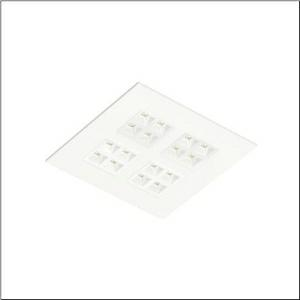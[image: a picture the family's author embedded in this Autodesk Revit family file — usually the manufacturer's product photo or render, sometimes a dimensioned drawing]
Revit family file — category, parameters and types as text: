
# Revit family: silica_r__31_square_51my6ndu34wa_7304
name_source: partatom
category: Lighting Fixtures
units: mm (PartAtom-declared; Revit-internal decimal feet)

## family parameters
Cut with Voids When Loaded = No
Host = Face
Light Source = No
Part Type = Normal
Room Calculation Point = No
Round Connector Dimension = Use Diameter
Shared = No

## types (1)
- --- (1 x LED, 6230 lm, 38.5 W, 3000K)
    Apparent Load = 39 VA
    CIE Flux Codes = 81 99 100 100 100
    Color Rendering = 80
    Color Temperature = 3000K
    Default Elevation = 1800 mm
    Description = Silica® 31 Square, office luminaire, primary light control with lens, of PMMA, primary anti-glare with reflector, of PC, white, light emission: direct distribution, primary light characteristic: symmetric, installation type: lay-in mounting, LED, rated luminous flux: 4.540lm, luminous efficacy: 162lm/W, light colour: 830, colour temperature: 3000K, control gear: DALI 2, Multilumen, with terminal, 5-pole, mains connection: 220..240V, AC, 50/60Hz, rated input power: 28W, luminaire housing, of sheet steel, coated, traffic white (RAL 9016), module: M625, length: 620mm, width: 620mm, height: 43mm, protection rating (complete): IP20, insulation class (complete): insulation class II (safety insulation), certification: CE, impact resistance: IK03, permissible operating ambient temperature: -20..+35°C, standard: EN 50419, packaging unit: 1 piece
    Height = 0 mm  [stored 0 ft]
    Lamp = 1 x LED
    Lamp Light Flux = 6230 lm
    Lamp Power = 38.5 W
    Lamp count = 1
    Length = 620 mm
    Luminous efficacy = 162 lm/W
    Manufacturer = Siteco
    ModVariant = No
    Model = 51MY6NDU34WA
    Mounting Place = Ceiling
    Mounting Type = Recessed
    Number of Poles = 1
    OnlyDefault = Yes
    Power Factor = 1
    Product Name = Silica® 31 Square
    Product group = office luminaire | ceiling recessed
    ProductGroupID = 401
    Protection Class = Protection class II
    Protection Degree = IP 20
    RLX_Detail_Level = 1
    RLX_Emergency_Light_Flux = 0 lm
    RLX_Emergency_Type = 0
    RLX_Emergency_Type_DB = No
    RlxData = <blob elided: 28117 chars, md5=bb4f251c>
    Socket = socket
    Standby Power = 0 W
    System Light Flux = 6230 lm
    System Power = 39 W
    Type Comments = factory setting: luminous flux: 100 % | (OFF | OFF | OFF | OFF) | 1050 mA
    Type Image = l_1313651.jpg
    URL = http://relux.com
    VarID = @adj_036046
    Voltage = 0 V
    Weight = 0.00 kg
    Width = 620 mm

note: [stored X ft] marks values corroborated as IEEE doubles in the binary element streams (Revit-internal decimal feet)

## geometry (parser evidence)
native form markers: Blend x4, Sweep x11
no freeform markers — native parametric forms only
